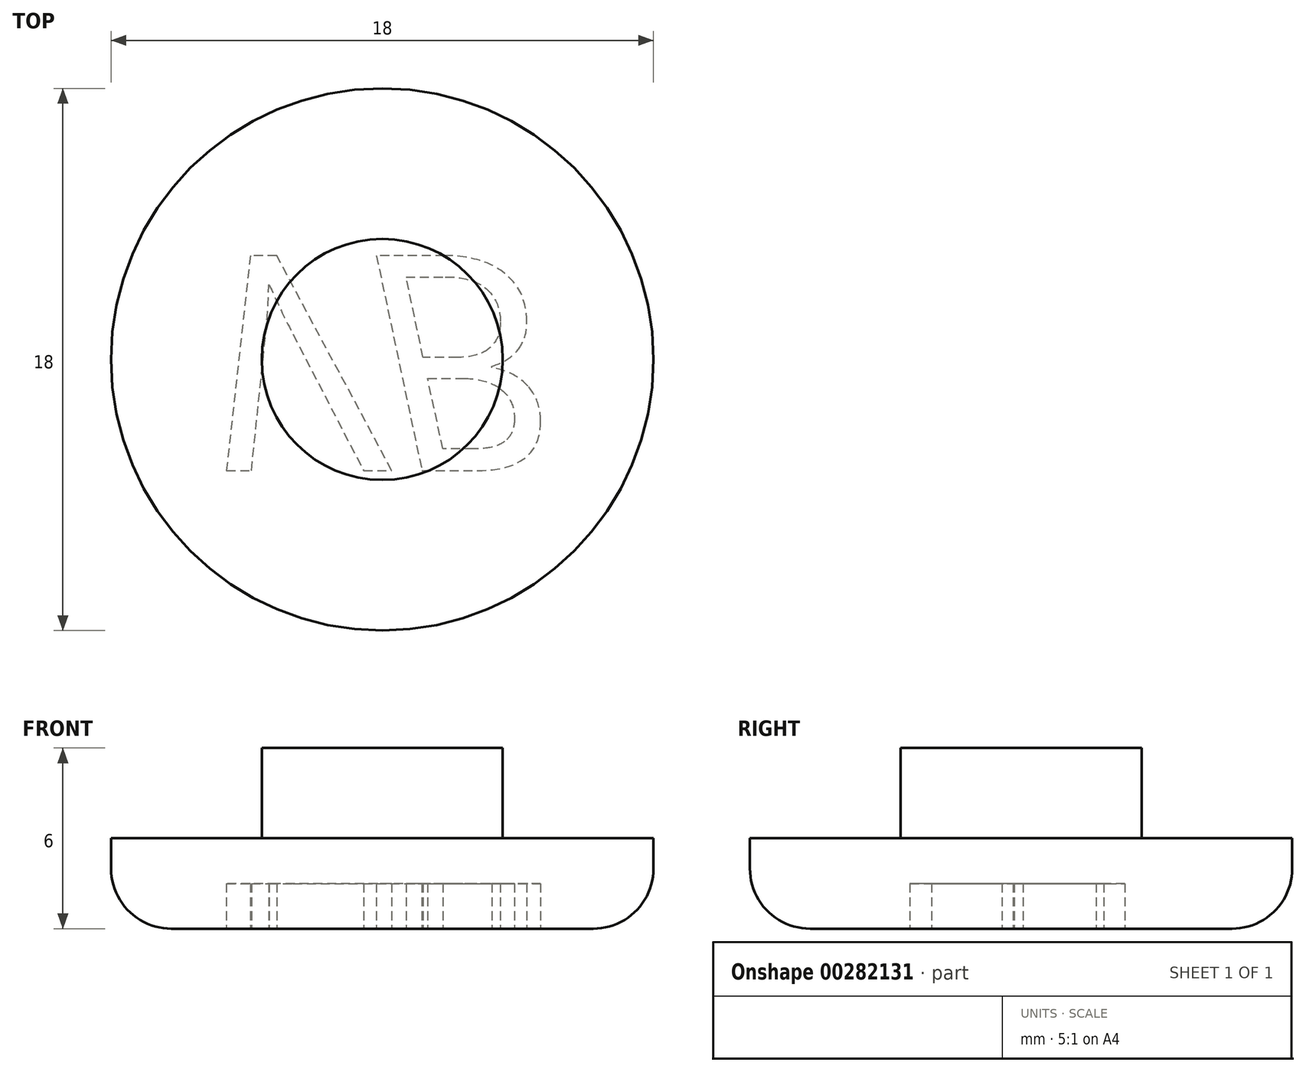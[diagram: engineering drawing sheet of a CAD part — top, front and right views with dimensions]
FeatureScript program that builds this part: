
annotation { "Feature Type Name" : "Feature", "Feature Type Description" : "" }
export const myFeature = defineFeature(function(context is Context, id is Id, definition is map)
    precondition{}
    {
        {
            var Q0;
            Q0=qCreatedBy(makeId("Top.planeOp"),FACE);
            var sketch = newSketch(context, id + "F0", { "sketchPlane" : qUnion([Q0])});
            skCircle(sketch, "E0", {"center": v(0, 0) * mm, "radius": 9 * mm});
            skSolve(sketch);
        }
        {
            var Q0;
            Q0=qSketchRegion(id+"F0",true);
            extrude(context, id + "F1", {"entities" : qUnion([Q0]), "depth" : 3 * mm});
        }
        {
            var Q0;
            Q0=makeQuery(id+"F1.opExtrude","CAP_FACE",FACE,{"disambiguationData":[OSD([sQuery(id+"F0.wireOp",EDGE,"E0")])],"isStart":false});
            var sketch = newSketch(context, id + "F2", { "sketchPlane" : qUnion([Q0])});
            skCircle(sketch, "E1", {"center": v(0, 0) * mm, "radius": 4 * mm});
            skSolve(sketch);
        }
        {
            var Q0;
            Q0=qSketchRegion(id+"F2",true);
            extrude(context, id + "F3", {"entities" : qUnion([Q0]), "operationType" : NewBodyOperationType.ADD, "depth" : 3 * mm, "offsetDistance" : 25 * mm});
        }
        {
            var Q0;
            Q0=makeQuery(id+"F1.opExtrude","CAP_EDGE",EDGE,{"disambiguationData":[OSD([sQuery(id+"F0.wireOp",EDGE,"E0")])],"isStart":true});
            fillet(context, id + "F4", {"entities" : qUnion([Q0]), "radius" : 2 * mm, "tangentPropagation" : true, "allowEdgeOverflow" : false});
        }
        {
            var Q0;
            Q0=makeQuery(id+"F1.opExtrude","CAP_FACE",FACE,{"disambiguationData":[OSD([sQuery(id+"F0.wireOp",EDGE,"E0")])],"isStart":true});
            var sketch = newSketch(context, id + "F5", { "sketchPlane" : qUnion([Q0])});
            skText(sketch, "E2", { "text": "VB", "fontName": "OpenSans-Italic.ttf"});
            const initialGuessF5  = {"E2": [-0.00609, -0.00345, 1, 0, 0.0072]};
            skSetInitialGuess(sketch, initialGuessF5);
            skSolve(sketch);
        }
        {
            var Q0;
            Q0 = qSketchRegion(id + "F5", true);
            extrude(context, id + "F6", {"entities" : qUnion([Q0]), "operationType" : NewBodyOperationType.REMOVE, "oppositeDirection" : true, "depth" : 1.5 * mm, "offsetDistance" : 25 * mm});
        }
    });
